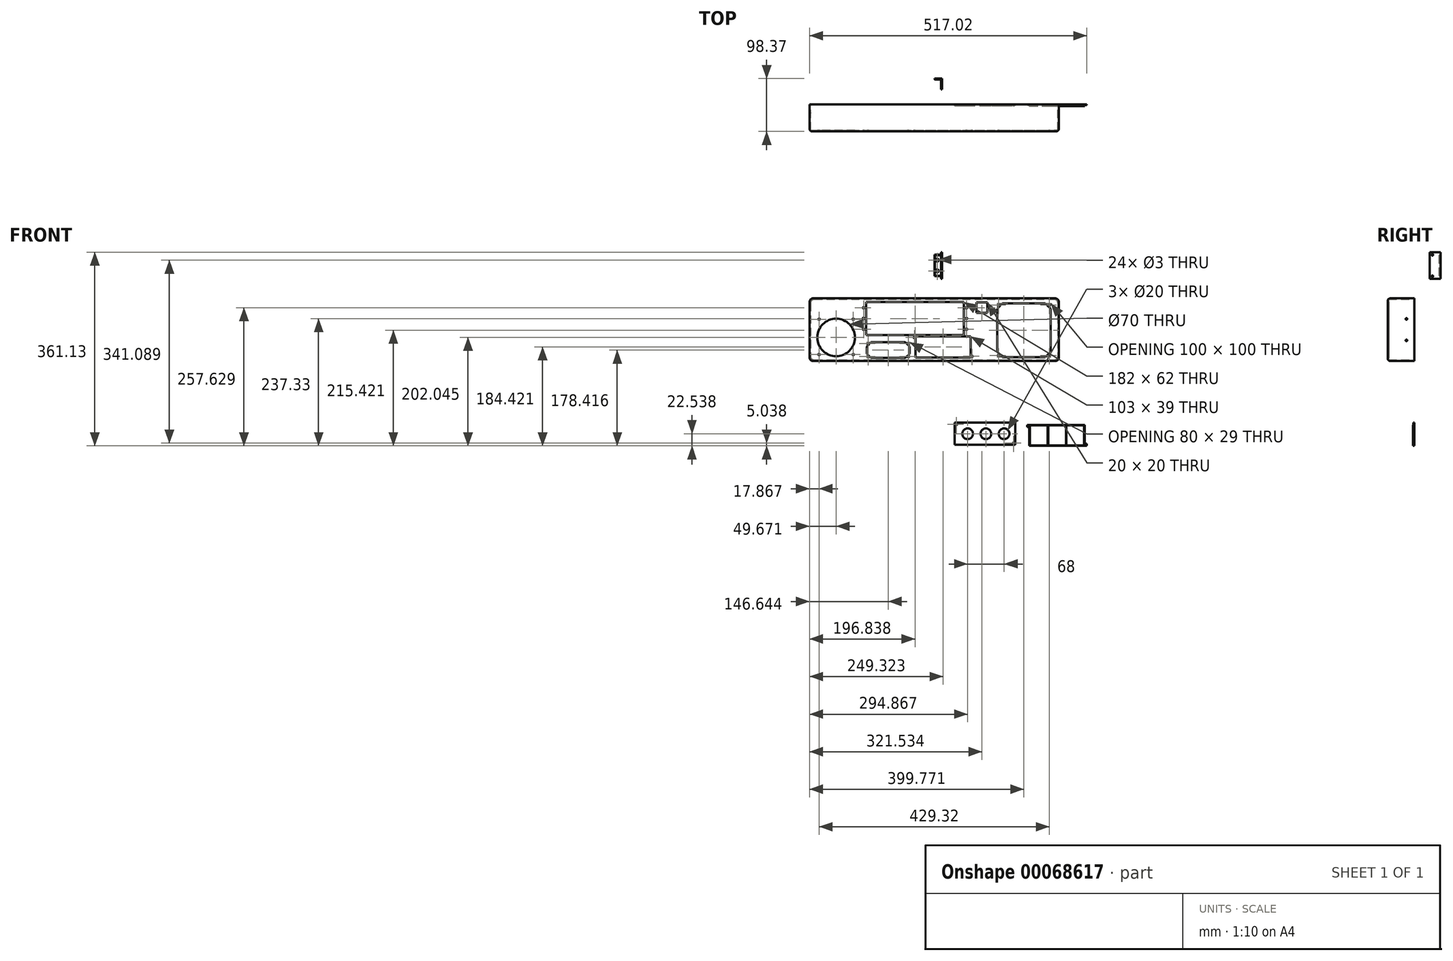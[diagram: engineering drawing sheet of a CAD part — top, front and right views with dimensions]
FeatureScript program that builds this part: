
annotation { "Feature Type Name" : "Feature", "Feature Type Description" : "" }
export const myFeature = defineFeature(function(context is Context, id is Id, definition is map)
    precondition{}
    {
        {
            var Q0;
            Q0=qCreatedBy(makeId("Front.planeOp"),FACE);
            var sketch = newSketch(context, id + "F0", { "sketchPlane" : qUnion([Q0])});
            skLineSegment(sketch, "E0.bottom", {"start": v(-245.15, 85.69) * mm, "end": v(219.85, 85.69) * mm});
            skLineSegment(sketch, "E0.top", {"start": v(-245.15, -31.31) * mm, "end": v(219.85, -31.31) * mm});
            skLineSegment(sketch, "E0.left", {"start": v(-245.15, 85.69) * mm, "end": v(-245.15, -31.31) * mm});
            skLineSegment(sketch, "E0.right", {"start": v(219.85, 85.69) * mm, "end": v(219.85, -31.31) * mm});
            skSolve(sketch);
        }
        {
            var Q0;
            Q0=qSketchRegion(id+"F0",true);
            var Q1;
            Q1=makeQuery(id+"F0.imprint","IMPRINT",FACE,{"disambiguationData":[TD([[makeQuery(id+"F0.imprint","IMPRINT",EDGE,{"derivedFrom":sQuery(id+"F0.wireOp",EDGE,"E0.bottom")}),-1.0]])]});
            extrude(context, id + "F1", {"entities" : qUnion([Q0, Q1]), "depth" : 50 * mm});
        }
        {
            var Q0;
            Q0=makeQuery(id+"F1.opExtrude","CAP_FACE",FACE,{"disambiguationData":[OSD([sQuery(id+"F0.wireOp",EDGE,"E0.bottom"),sQuery(id+"F0.wireOp",EDGE,"E0.top"),sQuery(id+"F0.wireOp",EDGE,"E0.left"),sQuery(id+"F0.wireOp",EDGE,"E0.right")])],"isStart":true});
            shell(context, id + "F2", {"entities" : qUnion([Q0]), "thickness" : 2 * mm});
        }
        {
            var Q0;
            Q0=makeQuery(id+"F1.opExtrude","CAP_FACE",FACE,{"disambiguationData":[OSD([sQuery(id+"F0.wireOp",EDGE,"E0.bottom"),sQuery(id+"F0.wireOp",EDGE,"E0.top"),sQuery(id+"F0.wireOp",EDGE,"E0.left"),sQuery(id+"F0.wireOp",EDGE,"E0.right")])],"isStart":false});
            var sketch = newSketch(context, id + "F3", { "sketchPlane" : qUnion([Q0])});
            skLineSegment(sketch, "E1.bottom", {"start": v(-139.31, 79.02) * mm, "end": v(42.69, 79.02) * mm});
            skLineSegment(sketch, "E1.top", {"start": v(-139.31, 17.02) * mm, "end": v(42.69, 17.02) * mm});
            skLineSegment(sketch, "E1.left", {"start": v(-139.31, 79.02) * mm, "end": v(-139.31, 17.02) * mm});
            skLineSegment(sketch, "E1.right", {"start": v(42.69, 79.02) * mm, "end": v(42.69, 17.02) * mm});
            skLineSegment(sketch, "E2.bottom", {"start": v(66.38, 78.32) * mm, "end": v(86.38, 78.32) * mm});
            skLineSegment(sketch, "E2.top", {"start": v(66.38, 58.32) * mm, "end": v(86.38, 58.32) * mm});
            skLineSegment(sketch, "E2.left", {"start": v(66.38, 78.32) * mm, "end": v(66.38, 58.32) * mm});
            skLineSegment(sketch, "E2.right", {"start": v(86.38, 78.32) * mm, "end": v(86.38, 58.32) * mm});
            skLineSegment(sketch, "E3.bottom", {"start": v(114.52, 76.11) * mm, "end": v(194.72, 76.11) * mm});
            skLineSegment(sketch, "E3.top", {"start": v(114.52, -23.89) * mm, "end": v(194.72, -23.89) * mm});
            skLineSegment(sketch, "E3.left", {"start": v(104.62, 66.21) * mm, "end": v(104.62, -13.99) * mm});
            skLineSegment(sketch, "E3.right", {"start": v(204.62, 66.21) * mm, "end": v(204.62, -13.99) * mm});
            skLineSegment(sketch, "E4.bottom", {"start": v(-128.05, -55.46) * mm, "end": v(-35.05, -55.46) * mm, "construction": true});
            skLineSegment(sketch, "E4.top", {"start": v(-128.05, -91.46) * mm, "end": v(-35.05, -91.46) * mm, "construction": true});
            skLineSegment(sketch, "E4.left", {"start": v(-128.05, -55.46) * mm, "end": v(-128.05, -91.46) * mm, "construction": true});
            skLineSegment(sketch, "E4.right", {"start": v(-35.05, -55.46) * mm, "end": v(-35.05, -91.46) * mm, "construction": true});
            skCircle(sketch, "E5", {"center": v(47.69, 68.02) * mm, "radius": 1.5 * mm});
            skCircle(sketch, "E6", {"center": v(47.69, 48.02) * mm, "radius": 1.5 * mm});
            skCircle(sketch, "E7", {"center": v(47.69, 28.02) * mm, "radius": 1.5 * mm});
            skLineSegment(sketch, "E8.bottom", {"start": v(-233.81, -59.67) * mm, "end": v(-156.81, -59.67) * mm, "construction": true});
            skLineSegment(sketch, "E8.top", {"start": v(-233.81, -136.67) * mm, "end": v(-156.81, -136.67) * mm, "construction": true});
            skLineSegment(sketch, "E8.left", {"start": v(-233.81, -59.67) * mm, "end": v(-233.81, -136.67) * mm, "construction": true});
            skLineSegment(sketch, "E8.right", {"start": v(-156.81, -59.67) * mm, "end": v(-156.81, -136.67) * mm, "construction": true});
            skCircle(sketch, "E9", {"center": v(107.52, 72.86) * mm, "radius": 1.5 * mm});
            skLineSegment(sketch, "E10", {"start": v(104.62, 66.21) * mm, "end": v(114.52, 76.11) * mm});
            skCircle(sketch, "E11", {"center": v(51.32, -84.07) * mm, "radius": 9.5 * mm});
            skLineSegment(sketch, "E12.bottom", {"start": v(34.38, -64.36) * mm, "end": v(127.38, -64.36) * mm});
            skLineSegment(sketch, "E12.top", {"start": v(34.38, -100.36) * mm, "end": v(127.38, -100.36) * mm});
            skLineSegment(sketch, "E12.left", {"start": v(34.38, -64.36) * mm, "end": v(34.38, -100.36) * mm});
            skLineSegment(sketch, "E12.right", {"start": v(127.38, -64.36) * mm, "end": v(127.38, -100.36) * mm});
            skCircle(sketch, "E13", {"center": v(81.35, -84.07) * mm, "radius": 9.5 * mm});
            skCircle(sketch, "E14", {"center": v(110.74, -84.07) * mm, "radius": 9.5 * mm});
            skCircle(sketch, "E15", {"center": v(38.38, -68.36) * mm, "radius": 1.5 * mm});
            skCircle(sketch, "E16", {"center": v(123.38, -96.36) * mm, "radius": 1.5 * mm});
            skLineSegment(sketch, "E17.bottom", {"start": v(-130.73, 3.6) * mm, "end": v(-66.28, 3.6) * mm});
            skLineSegment(sketch, "E17.top", {"start": v(-130.73, -25.4) * mm, "end": v(-66.28, -25.4) * mm});
            skLineSegment(sketch, "E17.left", {"start": v(-138.5, -4.17) * mm, "end": v(-138.5, -17.62) * mm});
            skLineSegment(sketch, "E17.right", {"start": v(-58.5, -4.17) * mm, "end": v(-58.5, -17.62) * mm});
            skCircle(sketch, "E18", {"center": v(-136, 1.1) * mm, "radius": 1.5 * mm});
            skCircle(sketch, "E19", {"center": v(-136, -22.9) * mm, "radius": 1.5 * mm});
            skCircle(sketch, "E20", {"center": v(-61, 1.1) * mm, "radius": 1.5 * mm});
            skCircle(sketch, "E21", {"center": v(-61, -22.9) * mm, "radius": 1.5 * mm});
            skLineSegment(sketch, "E22", {"start": v(104.62, -13.99) * mm, "end": v(114.52, -23.89) * mm});
            skLineSegment(sketch, "E23", {"start": v(194.72, -23.89) * mm, "end": v(204.62, -13.99) * mm});
            skLineSegment(sketch, "E24", {"start": v(194.72, 76.11) * mm, "end": v(204.62, 66.21) * mm});
            skCircle(sketch, "E25", {"center": v(107.52, -20.85) * mm, "radius": 1.5 * mm});
            skCircle(sketch, "E26", {"center": v(202.04, -20.85) * mm, "radius": 1.5 * mm});
            skCircle(sketch, "E27", {"center": v(202.04, 72.86) * mm, "radius": 1.5 * mm});
            skCircle(sketch, "E28", {"center": v(-195.48, 12.73) * mm, "radius": 35 * mm});
            skLineSegment(sketch, "E29", {"start": v(-138.5, -4.17) * mm, "end": v(-130.73, 3.6) * mm});
            skLineSegment(sketch, "E30", {"start": v(-66.28, 3.6) * mm, "end": v(-58.5, -4.17) * mm});
            skLineSegment(sketch, "E31", {"start": v(-58.5, -17.62) * mm, "end": v(-66.28, -25.4) * mm});
            skLineSegment(sketch, "E32", {"start": v(-138.5, -17.62) * mm, "end": v(-130.73, -25.4) * mm});
            skCircle(sketch, "E33", {"center": v(-144.31, 68.02) * mm, "radius": 1.5 * mm});
            skCircle(sketch, "E34", {"center": v(-144.31, 48.02) * mm, "radius": 1.5 * mm});
            skCircle(sketch, "E35", {"center": v(-144.31, 28.02) * mm, "radius": 1.5 * mm});
            skCircle(sketch, "E36", {"center": v(-227.28, 46.66) * mm, "radius": 1.5 * mm});
            skCircle(sketch, "E37", {"center": v(-227.28, -19.1) * mm, "radius": 1.5 * mm});
            skCircle(sketch, "E38", {"center": v(-163.64, -19.1) * mm, "radius": 1.5 * mm});
            skLineSegment(sketch, "E39.bottom", {"start": v(-52.33, 15.61) * mm, "end": v(60.67, 15.61) * mm, "construction": true});
            skLineSegment(sketch, "E39.top", {"start": v(-52.33, -25.39) * mm, "end": v(60.67, -25.39) * mm, "construction": true});
            skLineSegment(sketch, "E39.left", {"start": v(-52.33, 15.61) * mm, "end": v(-52.33, -25.39) * mm, "construction": true});
            skLineSegment(sketch, "E39.right", {"start": v(60.67, 15.61) * mm, "end": v(60.67, -25.39) * mm, "construction": true});
            skCircle(sketch, "E40", {"center": v(-163.68, 46.66) * mm, "radius": 1.5 * mm});
            skCircle(sketch, "E41", {"center": v(-49.33, 12.61) * mm, "radius": 1.5 * mm});
            skCircle(sketch, "E42", {"center": v(57.67, -22.39) * mm, "radius": 1.5 * mm});
            skLineSegment(sketch, "E43.bottom", {"start": v(-47.33, 14.61) * mm, "end": v(55.67, 14.61) * mm});
            skLineSegment(sketch, "E43.top", {"start": v(-47.33, -24.39) * mm, "end": v(55.67, -24.39) * mm});
            skLineSegment(sketch, "E43.left", {"start": v(-47.33, 14.61) * mm, "end": v(-47.33, -24.39) * mm});
            skLineSegment(sketch, "E43.right", {"start": v(55.67, 14.61) * mm, "end": v(55.67, -24.39) * mm});
            skPoint(sketch, "E44", {"position": v(-139.31, 48.02) * mm});
            skSolve(sketch);
        }
        {
            var Q0;
            Q0=makeQuery(id+"F1.opExtrude","SWEPT_EDGE",EDGE,{"disambiguationData":[OSD([sQuery(id+"F0.wireOp",EDGE,"E0.bottom"),sQuery(id+"F0.wireOp",EDGE,"E0.left")])]});
            var Q1;
            Q1=makeQuery(id+"F1.opExtrude","SWEPT_EDGE",EDGE,{"disambiguationData":[OSD([sQuery(id+"F0.wireOp",EDGE,"E0.bottom"),sQuery(id+"F0.wireOp",EDGE,"E0.right")])]});
            var Q2;
            Q2=makeQuery(id+"F1.opExtrude","SWEPT_EDGE",EDGE,{"disambiguationData":[OSD([sQuery(id+"F0.wireOp",EDGE,"E0.top"),sQuery(id+"F0.wireOp",EDGE,"E0.right")])]});
            var Q3;
            Q3=makeQuery(id+"F1.opExtrude","SWEPT_EDGE",EDGE,{"disambiguationData":[OSD([sQuery(id+"F0.wireOp",EDGE,"E0.top"),sQuery(id+"F0.wireOp",EDGE,"E0.left")])]});
            var Q4;
            Q4=makeQuery(id+"F2.opShell","OFFSET_EDGE",EDGE,{"disambiguationData":[OSD([sQuery(id+"F0.wireOp",EDGE,"E0.bottom"),sQuery(id+"F0.wireOp",EDGE,"E0.left")])]});
            var Q5;
            Q5=makeQuery(id+"F2.opShell","OFFSET_EDGE",EDGE,{"disambiguationData":[OSD([sQuery(id+"F0.wireOp",EDGE,"E0.top"),sQuery(id+"F0.wireOp",EDGE,"E0.left")])]});
            var Q6;
            Q6=makeQuery(id+"F2.opShell","OFFSET_EDGE",EDGE,{"disambiguationData":[OSD([sQuery(id+"F0.wireOp",EDGE,"E0.top"),sQuery(id+"F0.wireOp",EDGE,"E0.right")])]});
            var Q7;
            Q7=makeQuery(id+"F2.opShell","OFFSET_EDGE",EDGE,{"disambiguationData":[OSD([sQuery(id+"F0.wireOp",EDGE,"E0.bottom"),sQuery(id+"F0.wireOp",EDGE,"E0.right")])]});
            fillet(context, id + "F4", {"entities" : qUnion([Q0, Q1, Q2, Q3, Q4, Q5, Q6, Q7]), "radius" : 7 * mm, "tangentPropagation" : true, "allowEdgeOverflow" : false});
        }
        {
            var Q0;
            Q0 = qSketchRegion(id + "F3", true);
            extrude(context, id + "F5", {"entities" : qUnion([Q0]), "operationType" : NewBodyOperationType.REMOVE, "oppositeDirection" : true, "depth" : 25 * mm});
        }
        {
            var Q0;
            {var subQ0=sQuery(id+"F0.wireOp",EDGE,"E0.right");var subQ1=sQuery(id+"F0.wireOp",EDGE,"E0.bottom");Q0=makeQuery(id+"F4.opFillet","BLEND_EDGE",EDGE,{"blendedFrom":[makeQuery(id+"F1.opExtrude","SWEPT_EDGE",EDGE,{"disambiguationData":[OSD([subQ1,subQ0])]}),makeQuery(id+"F1.opExtrude","CAP_FACE",FACE,{"disambiguationData":[OSD([subQ1,sQuery(id+"F0.wireOp",EDGE,"E0.top"),sQuery(id+"F0.wireOp",EDGE,"E0.left"),subQ0])],"isStart":false})],"blendedInto":[makeQuery(id+"F1.opExtrude","CAP_FACE",FACE,{"disambiguationData":[OSD([subQ1,sQuery(id+"F0.wireOp",EDGE,"E0.top"),sQuery(id+"F0.wireOp",EDGE,"E0.left"),subQ0])],"isStart":false})]});}
            fillet(context, id + "F6", {"entities" : qUnion([Q0]), "radius" : 5 * mm, "tangentPropagation" : true, "allowEdgeOverflow" : false});
        }
        {
            var Q0;
            Q0=makeQuery(id+"F1.opExtrude","CAP_FACE",FACE,{"disambiguationData":[OSD([sQuery(id+"F0.wireOp",EDGE,"E0.bottom"),sQuery(id+"F0.wireOp",EDGE,"E0.top"),sQuery(id+"F0.wireOp",EDGE,"E0.left"),sQuery(id+"F0.wireOp",EDGE,"E0.right")])],"isStart":false});
            var sketch = newSketch(context, id + "F7", { "sketchPlane" : qUnion([Q0])});
            skLineSegment(sketch, "E45.bottom", {"start": v(216.55, -24.6) * mm, "end": v(89.55, -24.6) * mm});
            skLineSegment(sketch, "E45.top", {"start": v(216.55, 75.4) * mm, "end": v(89.55, 75.4) * mm});
            skLineSegment(sketch, "E45.left", {"start": v(216.55, -24.6) * mm, "end": v(216.55, 75.4) * mm});
            skLineSegment(sketch, "E45.right", {"start": v(89.55, -24.6) * mm, "end": v(89.55, 75.4) * mm});
            skLineSegment(sketch, "E46.bottom", {"start": v(-397.12, -53.44) * mm, "end": v(-332.84, -53.44) * mm});
            skLineSegment(sketch, "E46.top", {"start": v(-397.12, -159.24) * mm, "end": v(-332.84, -159.24) * mm});
            skLineSegment(sketch, "E46.left", {"start": v(-397.12, -53.44) * mm, "end": v(-397.12, -159.24) * mm});
            skLineSegment(sketch, "E46.right", {"start": v(-332.84, -53.44) * mm, "end": v(-332.84, -159.24) * mm});
            skLineSegment(sketch, "E47.bottom", {"start": v(38.72, -106.98) * mm, "end": v(60.72, -106.98) * mm, "construction": true});
            skLineSegment(sketch, "E47.top", {"start": v(38.72, -136.98) * mm, "end": v(60.72, -136.98) * mm, "construction": true});
            skLineSegment(sketch, "E47.left", {"start": v(38.72, -106.98) * mm, "end": v(38.72, -136.98) * mm, "construction": true});
            skLineSegment(sketch, "E47.right", {"start": v(60.72, -106.98) * mm, "end": v(60.72, -136.98) * mm, "construction": true});
            skLineSegment(sketch, "E48.bottom", {"start": v(-233.32, 80.69) * mm, "end": v(-155.32, 80.69) * mm});
            skLineSegment(sketch, "E48.top", {"start": v(-233.32, -26.31) * mm, "end": v(-155.32, -26.31) * mm});
            skLineSegment(sketch, "E48.left", {"start": v(-233.32, 80.69) * mm, "end": v(-233.32, -26.31) * mm});
            skLineSegment(sketch, "E48.right", {"start": v(-155.32, 80.69) * mm, "end": v(-155.32, -26.31) * mm});
            skLineSegment(sketch, "E49.bottom", {"start": v(31.72, -103.48) * mm, "end": v(64.72, -103.48) * mm, "construction": true});
            skLineSegment(sketch, "E49.top", {"start": v(31.72, -140.48) * mm, "end": v(64.72, -140.48) * mm, "construction": true});
            skLineSegment(sketch, "E49.left", {"start": v(31.72, -103.48) * mm, "end": v(31.72, -140.48) * mm, "construction": true});
            skLineSegment(sketch, "E49.right", {"start": v(64.72, -103.48) * mm, "end": v(64.72, -140.48) * mm, "construction": true});
            skLineSegment(sketch, "E50.bottom", {"start": v(72.72, -106.98) * mm, "end": v(94.72, -106.98) * mm, "construction": true});
            skLineSegment(sketch, "E50.top", {"start": v(72.72, -136.98) * mm, "end": v(94.72, -136.98) * mm, "construction": true});
            skLineSegment(sketch, "E50.left", {"start": v(72.72, -106.98) * mm, "end": v(72.72, -136.98) * mm, "construction": true});
            skLineSegment(sketch, "E50.right", {"start": v(94.72, -106.98) * mm, "end": v(94.72, -136.98) * mm, "construction": true});
            skLineSegment(sketch, "E51.bottom", {"start": v(65.72, -103.48) * mm, "end": v(98.72, -103.48) * mm, "construction": true});
            skLineSegment(sketch, "E51.top", {"start": v(65.72, -140.48) * mm, "end": v(98.72, -140.48) * mm, "construction": true});
            skLineSegment(sketch, "E51.left", {"start": v(65.72, -103.48) * mm, "end": v(65.72, -140.48) * mm, "construction": true});
            skLineSegment(sketch, "E51.right", {"start": v(98.72, -103.48) * mm, "end": v(98.72, -140.48) * mm, "construction": true});
            skLineSegment(sketch, "E52.bottom", {"start": v(106.72, -106.98) * mm, "end": v(128.72, -106.98) * mm, "construction": true});
            skLineSegment(sketch, "E52.top", {"start": v(106.72, -136.98) * mm, "end": v(128.72, -136.98) * mm, "construction": true});
            skLineSegment(sketch, "E52.left", {"start": v(106.72, -106.98) * mm, "end": v(106.72, -136.98) * mm, "construction": true});
            skLineSegment(sketch, "E52.right", {"start": v(128.72, -106.98) * mm, "end": v(128.72, -136.98) * mm, "construction": true});
            skLineSegment(sketch, "E53.bottom", {"start": v(99.72, -103.48) * mm, "end": v(132.72, -103.48) * mm, "construction": true});
            skLineSegment(sketch, "E53.top", {"start": v(99.72, -140.48) * mm, "end": v(132.72, -140.48) * mm, "construction": true});
            skLineSegment(sketch, "E53.left", {"start": v(99.72, -103.48) * mm, "end": v(99.72, -140.48) * mm, "construction": true});
            skLineSegment(sketch, "E53.right", {"start": v(132.72, -103.48) * mm, "end": v(132.72, -140.48) * mm, "construction": true});
            skCircle(sketch, "E54", {"center": v(83.72, -121.98) * mm, "radius": 10 * mm});
            skCircle(sketch, "E55", {"center": v(49.72, -121.98) * mm, "radius": 10 * mm});
            skCircle(sketch, "E56", {"center": v(117.72, -121.98) * mm, "radius": 10 * mm});
            skLineSegment(sketch, "E57.bottom", {"start": v(-253.6, -26.31) * mm, "end": v(-331.6, -26.31) * mm});
            skLineSegment(sketch, "E57.top", {"start": v(-253.6, 93.69) * mm, "end": v(-331.6, 93.69) * mm});
            skLineSegment(sketch, "E57.left", {"start": v(-253.6, -26.31) * mm, "end": v(-253.6, 93.69) * mm});
            skLineSegment(sketch, "E57.right", {"start": v(-331.6, -26.31) * mm, "end": v(-331.6, 93.69) * mm});
            skSolve(sketch);
        }
        {
            var Q0;
            Q0=makeQuery(id+"F1.opExtrude","SWEPT_FACE",FACE,{"disambiguationData":[OSD([sQuery(id+"F0.wireOp",EDGE,"E0.left")])]});
            var sketch = newSketch(context, id + "F8", { "sketchPlane" : qUnion([Q0])});
            skCircle(sketch, "E58", {"center": v(15, 47.19) * mm, "radius": 1.5 * mm});
            skCircle(sketch, "E59", {"center": v(15, 7.19) * mm, "radius": 1.5 * mm});
            skLineSegment(sketch, "E60", {"start": v(-16.01, 27.19) * mm, "end": v(37.35, 27.19) * mm, "construction": true});
            skPoint(sketch, "E61.middle.positionSnap0", {"position": v(0, 27.19) * mm});
            skPoint(sketch, "E61.centerSnap0", {"position": v(0, 27.19) * mm});
            skLineSegment(sketch, "E62.bottom", {"start": v(3, 6.19) * mm, "end": v(0, 6.19) * mm, "construction": true});
            skLineSegment(sketch, "E62.top", {"start": v(3, 48.19) * mm, "end": v(0, 48.19) * mm, "construction": true});
            skLineSegment(sketch, "E62.left", {"start": v(3, 6.19) * mm, "end": v(3, 48.19) * mm, "construction": true});
            skLineSegment(sketch, "E62.right", {"start": v(0, 6.19) * mm, "end": v(0, 48.19) * mm, "construction": true});
            skPoint(sketch, "E62.middle", {"position": v(1.5, 27.19) * mm});
            skSolve(sketch);
        }
        {
            var Q0;
            Q0 = qSketchRegion(id + "F8", true);
            extrude(context, id + "F9", {"entities" : qUnion([Q0]), "operationType" : NewBodyOperationType.REMOVE, "oppositeDirection" : true, "depth" : 500 * mm});
        }
        {
            var Q0;
            Q0=qCreatedBy(makeId("Right.planeOp"),FACE);
            var sketch = newSketch(context, id + "F10", { "sketchPlane" : qUnion([Q0])});
            skLineSegment(sketch, "E63.bottom", {"start": v(28.37, 121.82) * mm, "end": v(48.37, 121.82) * mm});
            skLineSegment(sketch, "E63.top", {"start": v(28.37, 171.82) * mm, "end": v(48.37, 171.82) * mm});
            skLineSegment(sketch, "E63.left", {"start": v(28.37, 121.82) * mm, "end": v(28.37, 171.82) * mm});
            skLineSegment(sketch, "E63.right", {"start": v(48.37, 121.82) * mm, "end": v(48.37, 171.82) * mm});
            skPoint(sketch, "E63.middle", {"position": v(38.37, 146.82) * mm});
            skCircle(sketch, "E64", {"center": v(33.37, 166.82) * mm, "radius": 1.5 * mm});
            skCircle(sketch, "E65", {"center": v(33.37, 126.82) * mm, "radius": 1.5 * mm});
            skSolve(sketch);
        }
        {
            var Q0;
            Q0 = qSketchRegion(id + "F10", true);
            extrude(context, id + "F11", {"entities" : qUnion([Q0]), "depth" : 2 * mm});
        }
        {
            var Q0;
            Q0=makeQuery(id+"F11.opExtrude","SWEPT_FACE",FACE,{"disambiguationData":[OSD([sQuery(id+"F10.wireOp",EDGE,"E63.right")])]});
            var sketch = newSketch(context, id + "F12", { "sketchPlane" : qUnion([Q0])});
            skLineSegment(sketch, "E66.bottom", {"start": v(0, 166.82) * mm, "end": v(12, 166.82) * mm});
            skLineSegment(sketch, "E66.top", {"start": v(0, 126.82) * mm, "end": v(12, 126.82) * mm});
            skLineSegment(sketch, "E66.left", {"start": v(0, 166.82) * mm, "end": v(0, 126.82) * mm});
            skLineSegment(sketch, "E66.right", {"start": v(12, 166.82) * mm, "end": v(12, 126.82) * mm});
            skSolve(sketch);
        }
        {
            var Q0;
            Q0 = qSketchRegion(id + "F12", true);
            extrude(context, id + "F13", {"entities" : qUnion([Q0]), "operationType" : NewBodyOperationType.ADD, "oppositeDirection" : true, "depth" : 2 * mm});
        }
        {
            var Q0;
            Q0=makeQuery(id+"F13.opExtrude","CAP_FACE",FACE,{"disambiguationData":[OSD([sQuery(id+"F12.wireOp",EDGE,"E66.bottom"),sQuery(id+"F12.wireOp",EDGE,"E66.top"),sQuery(id+"F12.wireOp",EDGE,"E66.left"),sQuery(id+"F12.wireOp",EDGE,"E66.right")])],"isStart":false});
            var sketch = newSketch(context, id + "F14", { "sketchPlane" : qUnion([Q0])});
            skCircle(sketch, "E67", {"center": v(-7, 156.82) * mm, "radius": 1.5 * mm});
            skCircle(sketch, "E68", {"center": v(-7, 136.82) * mm, "radius": 1.5 * mm});
            skSolve(sketch);
        }
        {
            var Q0;
            Q0=sQuery(id+"F14.wireOp",VERTEX,"E67.center");
            var Q1;
            Q1=sQuery(id+"F14.wireOp",VERTEX,"E68.center");
            var Q2;
            Q2=makeQuery(id+"F11.opExtrude","SWEPT_BODY",BODY,{"disambiguationData":[OSD([sQuery(id+"F10.wireOp",EDGE,"E63.bottom"),sQuery(id+"F10.wireOp",EDGE,"E63.top"),sQuery(id+"F10.wireOp",EDGE,"E63.left"),sQuery(id+"F10.wireOp",EDGE,"E63.right"),sQuery(id+"F10.wireOp",EDGE,"E64"),sQuery(id+"F10.wireOp",EDGE,"E65")])]});
            hole(context, id + "F15", {"style" : HoleStyle.C_SINK, "endStyle" : HoleEndStyle.THROUGH, "holeDiameter" : 3 * mm, "cSinkDiameter" : 5.7 * mm, "cSinkAngle" : 90 * degree, "locations" : qUnion([Q0, Q1]), "scope" : qUnion([Q2]), "isTappedThrough" : true});
        }
        {
            var Q0;
            Q0=makeQuery(id+"F13.opExtrude","CAP_EDGE",EDGE,{"disambiguationData":[OSD([sQuery(id+"F12.wireOp",EDGE,"E66.bottom")])],"isStart":false});
            var Q1;
            Q1=makeQuery(id+"F13.opExtrude","CAP_EDGE",EDGE,{"disambiguationData":[OSD([sQuery(id+"F12.wireOp",EDGE,"E66.right")])],"isStart":false});
            var Q2;
            Q2=makeQuery(id+"F13.opExtrude","CAP_EDGE",EDGE,{"disambiguationData":[OSD([sQuery(id+"F12.wireOp",EDGE,"E66.top")])],"isStart":false});
            chamfer(context, id + "F16", {"entities" : qUnion([Q0, Q1, Q2]), "width" : 1 * mm, "tangentPropagation" : true});
        }
        {
            var Q0;
            Q0=qCreatedBy(makeId("Front.planeOp"),FACE);
            var sketch = newSketch(context, id + "F17", { "sketchPlane" : qUnion([Q0])});
            skCircle(sketch, "E69", {"center": v(49.72, -166.77) * mm, "radius": 10 * mm});
            skCircle(sketch, "E70", {"center": v(83.72, -166.77) * mm, "radius": 10 * mm});
            skCircle(sketch, "E71", {"center": v(117.72, -166.77) * mm, "radius": 10 * mm});
            skCircle(sketch, "E72", {"center": v(28.72, -149.27) * mm, "radius": 1.5 * mm});
            skCircle(sketch, "E73", {"center": v(135.72, -184.27) * mm, "radius": 1.5 * mm});
            skLineSegment(sketch, "E74.bottom", {"start": v(25.72, -146.27) * mm, "end": v(138.72, -146.27) * mm});
            skLineSegment(sketch, "E74.top", {"start": v(25.72, -187.27) * mm, "end": v(138.72, -187.27) * mm});
            skLineSegment(sketch, "E74.left", {"start": v(25.72, -146.27) * mm, "end": v(25.72, -187.27) * mm});
            skLineSegment(sketch, "E74.right", {"start": v(138.72, -146.27) * mm, "end": v(138.72, -187.27) * mm});
            skSolve(sketch);
        }
        {
            var Q0;
            Q0=makeQuery(id+"F17.imprint","IMPRINT",FACE,{"disambiguationData":[TD([[makeQuery(id+"F17.imprint","IMPRINT",EDGE,{"derivedFrom":sQuery(id+"F17.wireOp",EDGE,"E69")}),-1.0]])]});
            extrude(context, id + "F18", {"entities" : qUnion([Q0]), "depth" : 2 * mm});
        }
        {
            var Q0;
            Q0=qCreatedBy(makeId("Front.planeOp"),FACE);
            var sketch = newSketch(context, id + "F19", { "sketchPlane" : qUnion([Q0])});
            skLineSegment(sketch, "E75.bottom", {"start": v(164.87, -150.31) * mm, "end": v(267.87, -150.31) * mm});
            skLineSegment(sketch, "E75.top", {"start": v(164.87, -189.31) * mm, "end": v(267.87, -189.31) * mm});
            skLineSegment(sketch, "E75.left", {"start": v(164.87, -150.31) * mm, "end": v(164.87, -189.31) * mm});
            skLineSegment(sketch, "E75.right", {"start": v(267.87, -150.31) * mm, "end": v(267.87, -189.31) * mm});
            skLineSegment(sketch, "E76.bottom", {"start": v(164.87, -150.31) * mm, "end": v(160.87, -150.31) * mm});
            skLineSegment(sketch, "E76.top", {"start": v(164.87, -154.31) * mm, "end": v(160.87, -154.31) * mm});
            skLineSegment(sketch, "E76.left", {"start": v(164.87, -150.31) * mm, "end": v(164.87, -154.31) * mm});
            skLineSegment(sketch, "E76.right", {"start": v(160.87, -150.31) * mm, "end": v(160.87, -154.31) * mm});
            skLineSegment(sketch, "E77.bottom", {"start": v(267.87, -189.31) * mm, "end": v(271.87, -189.31) * mm});
            skLineSegment(sketch, "E77.top", {"start": v(267.87, -185.31) * mm, "end": v(271.87, -185.31) * mm});
            skLineSegment(sketch, "E77.left", {"start": v(267.87, -189.31) * mm, "end": v(267.87, -185.31) * mm});
            skLineSegment(sketch, "E77.right", {"start": v(271.87, -189.31) * mm, "end": v(271.87, -185.31) * mm});
            skCircle(sketch, "E78", {"center": v(162.87, -152.31) * mm, "radius": 1.5 * mm});
            skCircle(sketch, "E79", {"center": v(269.87, -187.31) * mm, "radius": 1.5 * mm});
            skSolve(sketch);
        }
        {
            var Q0;
            Q0=makeQuery(id+"F19.imprint","IMPRINT",FACE,{"disambiguationData":[TD([[makeQuery(id+"F19.imprint","IMPRINT",EDGE,{"derivedFrom":sQuery(id+"F19.wireOp",EDGE,"E75.bottom")}),-1.0]])]});
            extrude(context, id + "F20", {"entities" : qUnion([Q0]), "depth" : 3 * mm});
        }
        {
            var Q0;
            Q0=makeQuery(id+"F19.imprint","IMPRINT",FACE,{"disambiguationData":[TD([[makeQuery(id+"F19.imprint","IMPRINT",EDGE,{"derivedFrom":sQuery(id+"F19.wireOp",EDGE,"E76.bottom")}),1.0]])]});
            var Q1;
            Q1=makeQuery(id+"F19.imprint","IMPRINT",FACE,{"disambiguationData":[TD([[makeQuery(id+"F19.imprint","IMPRINT",EDGE,{"derivedFrom":sQuery(id+"F19.wireOp",EDGE,"E77.bottom")}),1.0]])]});
            extrude(context, id + "F21", {"entities" : qUnion([Q0, Q1]), "operationType" : NewBodyOperationType.ADD, "depth" : 1 * mm});
        }
        {
            var Q0;
            Q0=makeQuery(id+"F20.opExtrude","CAP_FACE",FACE,{"disambiguationData":[OSD([sQuery(id+"F19.wireOp",EDGE,"E75.bottom"),sQuery(id+"F19.wireOp",EDGE,"E75.top"),sQuery(id+"F19.wireOp",EDGE,"E75.left"),sQuery(id+"F19.wireOp",EDGE,"E75.right"),sQuery(id+"F19.wireOp",EDGE,"E76.left"),sQuery(id+"F19.wireOp",EDGE,"E77.left")])],"isStart":false});
            var sketch = newSketch(context, id + "F22", { "sketchPlane" : qUnion([Q0])});
            skLineSegment(sketch, "E80.bottom", {"start": v(165.87, -151.31) * mm, "end": v(198.87, -151.31) * mm});
            skLineSegment(sketch, "E80.top", {"start": v(165.87, -188.31) * mm, "end": v(198.87, -188.31) * mm});
            skLineSegment(sketch, "E80.left", {"start": v(165.87, -151.31) * mm, "end": v(165.87, -188.31) * mm});
            skLineSegment(sketch, "E80.right", {"start": v(198.87, -151.31) * mm, "end": v(198.87, -188.31) * mm});
            skLineSegment(sketch, "E81.bottom", {"start": v(199.87, -151.31) * mm, "end": v(232.87, -151.31) * mm});
            skLineSegment(sketch, "E81.top", {"start": v(199.87, -188.31) * mm, "end": v(232.87, -188.31) * mm});
            skLineSegment(sketch, "E81.left", {"start": v(199.87, -151.31) * mm, "end": v(199.87, -188.31) * mm});
            skLineSegment(sketch, "E81.right", {"start": v(232.87, -151.31) * mm, "end": v(232.87, -188.31) * mm});
            skLineSegment(sketch, "E82.bottom", {"start": v(233.87, -151.31) * mm, "end": v(266.87, -151.31) * mm});
            skLineSegment(sketch, "E82.top", {"start": v(233.87, -188.31) * mm, "end": v(266.87, -188.31) * mm});
            skLineSegment(sketch, "E82.left", {"start": v(233.87, -151.31) * mm, "end": v(233.87, -188.31) * mm});
            skLineSegment(sketch, "E82.right", {"start": v(266.87, -151.31) * mm, "end": v(266.87, -188.31) * mm});
            skLineSegment(sketch, "E83.bottom", {"start": v(198.87, -161.31) * mm, "end": v(199.87, -161.31) * mm});
            skLineSegment(sketch, "E83.top", {"start": v(198.87, -178.31) * mm, "end": v(199.87, -178.31) * mm});
            skLineSegment(sketch, "E83.left", {"start": v(198.87, -161.31) * mm, "end": v(198.87, -178.31) * mm});
            skLineSegment(sketch, "E83.right", {"start": v(199.87, -161.31) * mm, "end": v(199.87, -178.31) * mm});
            skLineSegment(sketch, "E84.bottom", {"start": v(232.87, -161.31) * mm, "end": v(233.87, -161.31) * mm});
            skLineSegment(sketch, "E84.top", {"start": v(232.87, -178.31) * mm, "end": v(233.87, -178.31) * mm});
            skLineSegment(sketch, "E84.left", {"start": v(232.87, -161.31) * mm, "end": v(232.87, -178.31) * mm});
            skLineSegment(sketch, "E84.right", {"start": v(233.87, -161.31) * mm, "end": v(233.87, -178.31) * mm});
            skSolve(sketch);
        }
        {
            var Q0;
            {var subQ1=sQuery(id+"F22.wireOp",EDGE,"E80.bottom");Q0=makeQuery(id+"F22.imprint","IMPRINT",FACE,{"disambiguationData":[TD([[makeQuery(id+"F22.imprint","IMPRINT",EDGE,{"derivedFrom":subQ1}),-1.0]])]});}
            var Q1;
            {var subQ3=sQuery(id+"F22.wireOp",EDGE,"E81.bottom");Q1=makeQuery(id+"F22.imprint","IMPRINT",FACE,{"disambiguationData":[TD([[makeQuery(id+"F22.imprint","IMPRINT",EDGE,{"derivedFrom":subQ3}),-1.0]])]});}
            var Q2;
            {var subQ1=sQuery(id+"F22.wireOp",EDGE,"E82.bottom");Q2=makeQuery(id+"F22.imprint","IMPRINT",FACE,{"disambiguationData":[TD([[makeQuery(id+"F22.imprint","IMPRINT",EDGE,{"derivedFrom":subQ1}),-1.0]])]});}
            extrude(context, id + "F23", {"entities" : qUnion([Q0, Q1, Q2]), "operationType" : NewBodyOperationType.REMOVE, "oppositeDirection" : true, "depth" : 2 * mm});
        }
        {
            var Q0;
            Q0=makeQuery(id+"F22.imprint","IMPRINT",FACE,{"disambiguationData":[TD([[makeQuery(id+"F22.imprint","IMPRINT",EDGE,{"derivedFrom":sQuery(id+"F22.wireOp",EDGE,"E83.bottom")}),-1.0]])]});
            var Q1;
            Q1=makeQuery(id+"F22.imprint","IMPRINT",FACE,{"disambiguationData":[TD([[makeQuery(id+"F22.imprint","IMPRINT",EDGE,{"derivedFrom":sQuery(id+"F22.wireOp",EDGE,"E84.bottom")}),-1.0]])]});
            extrude(context, id + "F24", {"entities" : qUnion([Q0, Q1]), "operationType" : NewBodyOperationType.REMOVE, "oppositeDirection" : true, "depth" : 3 * mm});
        }
    });
